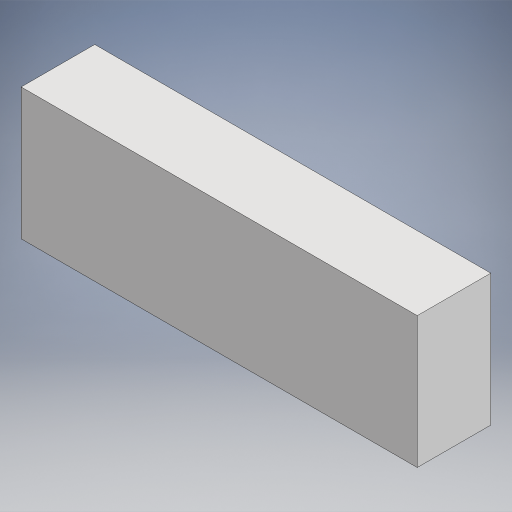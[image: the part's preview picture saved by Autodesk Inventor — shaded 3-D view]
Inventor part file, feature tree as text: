
AUTODESK INVENTOR PART (.ipt)
format: ipt  version: 2023.2 (Build 272271000, 271)  size: 193,024 bytes
history: native  units: in
note: dims shown in document units (in); Inventor stores cm internally (conversion verified against a paired STEP export)
features: extrude x1, sketch x1
ambient origin geometry x8: Origin, YZ Plane, XZ Plane, XY Plane, X Axis, Y Axis, Z Axis, Center Point
bodies: Solid1 (feature_tree)
feature tree (2):
  extrude  "Extrusion1"  Depth=6.5in
  sketch  "Sketch2"  dims[d3=11.625in d4=6.5in d5=35.0in d6=0.0in]
